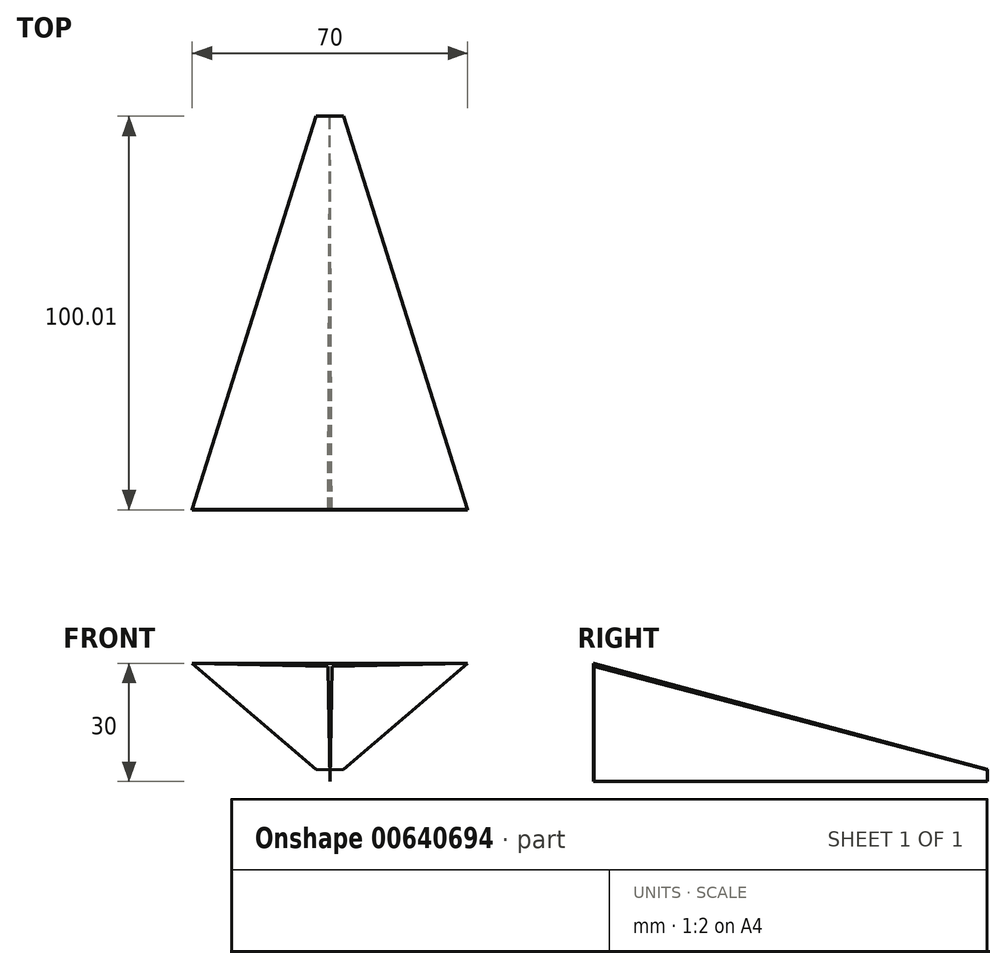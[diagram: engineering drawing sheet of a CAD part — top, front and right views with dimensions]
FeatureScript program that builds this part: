
annotation { "Feature Type Name" : "Feature", "Feature Type Description" : "" }
export const myFeature = defineFeature(function(context is Context, id is Id, definition is map)
    precondition{}
    {
        {
            var Q0;
            Q0=qCreatedBy(makeId("Front.planeOp"),FACE);
            var sketch = newSketch(context, id + "F0", { "sketchPlane" : qUnion([Q0])});
            skLineSegment(sketch, "E0", {"start": v(0, 30) * mm, "end": v(-35, 30) * mm});
            skLineSegment(sketch, "E1", {"start": v(0, 30) * mm, "end": v(35, 30) * mm});
            skLineSegment(sketch, "E2", {"start": v(35, 30) * mm, "end": v(0.5, 29.2) * mm});
            skLineSegment(sketch, "E3", {"start": v(-0.5, 29.2) * mm, "end": v(-35, 30) * mm});
            skLineSegment(sketch, "E4", {"start": v(0.5, 29.2) * mm, "end": v(0, 0) * mm});
            skLineSegment(sketch, "E5", {"start": v(0, 0) * mm, "end": v(-0.5, 29.2) * mm});
            skSolve(sketch);
        }
        {
            var Q0;
            Q0=qCreatedBy(makeId("Front.planeOp"),FACE);
            cPlane(context, id + "F1", {"entities" : qUnion([Q0]), "cplaneType" : CPlaneType.OFFSET, "offset" : 100 * mm, "oppositeDirection" : true, "width" : 150 * mm, "height" : 150 * mm});
        }
        {
            var Q0;
            Q0=qCreatedBy(id+"F1.planeOp",FACE);
            var sketch = newSketch(context, id + "F2", { "sketchPlane" : qUnion([Q0])});
            skLineSegment(sketch, "E6", {"start": v(0, 30) * mm, "end": v(-35, 30) * mm});
            skLineSegment(sketch, "E7", {"start": v(0, 30) * mm, "end": v(35, 30) * mm});
            skLineSegment(sketch, "E8", {"start": v(35, 30) * mm, "end": v(0.5, 29.2) * mm});
            skLineSegment(sketch, "E9", {"start": v(-0.5, 29.2) * mm, "end": v(-35, 30) * mm});
            skLineSegment(sketch, "E10", {"start": v(0.5, 29.2) * mm, "end": v(0, 0) * mm});
            skLineSegment(sketch, "E11", {"start": v(0, 0) * mm, "end": v(-0.5, 29.2) * mm});
            skSolve(sketch);
        }
        {
            var Q0;
            Q0=makeQuery(id+"F0.imprint","IMPRINT",FACE,{"disambiguationData":[TD([[makeQuery(id+"F0.imprint","IMPRINT",EDGE,{"derivedFrom":sQuery(id+"F0.wireOp",EDGE,"E0")}),1.0]])]});
            extrude(context, id + "F3", {"entities" : qUnion([Q0]), "depth" : .1 * mm, "offsetDistance" : 25 * mm});
        }
        {
            var Q0;
            Q0=makeQuery(id+"F2.imprint","IMPRINT",FACE,{"disambiguationData":[TD([[makeQuery(id+"F2.imprint","IMPRINT",EDGE,{"derivedFrom":sQuery(id+"F2.wireOp",EDGE,"E6")}),1.0]])]});
            extrude(context, id + "F4", {"entities" : qUnion([Q0]), "depth" : .1 * mm, "offsetDistance" : 25 * mm});
        }
        {
            var Q0;
            Q0=makeQuery(id+"F4.opExtrude","SWEPT_BODY",BODY,{"disambiguationData":[OSD([sQuery(id+"F2.wireOp",EDGE,"E6"),sQuery(id+"F2.wireOp",EDGE,"E7"),sQuery(id+"F2.wireOp",EDGE,"E8"),sQuery(id+"F2.wireOp",EDGE,"E9"),sQuery(id+"F2.wireOp",EDGE,"E10"),sQuery(id+"F2.wireOp",EDGE,"E11")])]});
            var Q1;
            Q1=makeQuery(id+"F4.opExtrude","CAP_VERTEX",VERTEX,{"disambiguationData":[OSD([sQuery(id+"F2.wireOp",EDGE,"E10"),sQuery(id+"F2.wireOp",EDGE,"E11")])],"isStart":false});
            transform(context, id + "F5", {"entities" : qUnion([Q0]), "transformType" : TransformType.SCALE_UNIFORMLY, "scale" : .1, "scalePoint" : qUnion([Q1]), "makeCopy" : false});
        }
        {
            var Q0;
            Q0=makeQuery(id+"F3.opExtrude","CAP_FACE",FACE,{"disambiguationData":[OSD([sQuery(id+"F0.wireOp",EDGE,"E0"),sQuery(id+"F0.wireOp",EDGE,"E1"),sQuery(id+"F0.wireOp",EDGE,"E2"),sQuery(id+"F0.wireOp",EDGE,"E3"),sQuery(id+"F0.wireOp",EDGE,"E4"),sQuery(id+"F0.wireOp",EDGE,"E5")])],"isStart":true});
            var Q1;
            Q1=makeQuery(id+"F4.opExtrude","CAP_FACE",FACE,{"disambiguationData":[OSD([sQuery(id+"F2.wireOp",EDGE,"E6"),sQuery(id+"F2.wireOp",EDGE,"E7"),sQuery(id+"F2.wireOp",EDGE,"E8"),sQuery(id+"F2.wireOp",EDGE,"E9"),sQuery(id+"F2.wireOp",EDGE,"E10"),sQuery(id+"F2.wireOp",EDGE,"E11")])],"isStart":false});
            loft(context, id + "F6", {"sheetProfilesArray" : [{ "sheetProfileEntities" : qUnion([Q0]) }, { "sheetProfileEntities" : qUnion([Q1]) }]});
        }
    });
